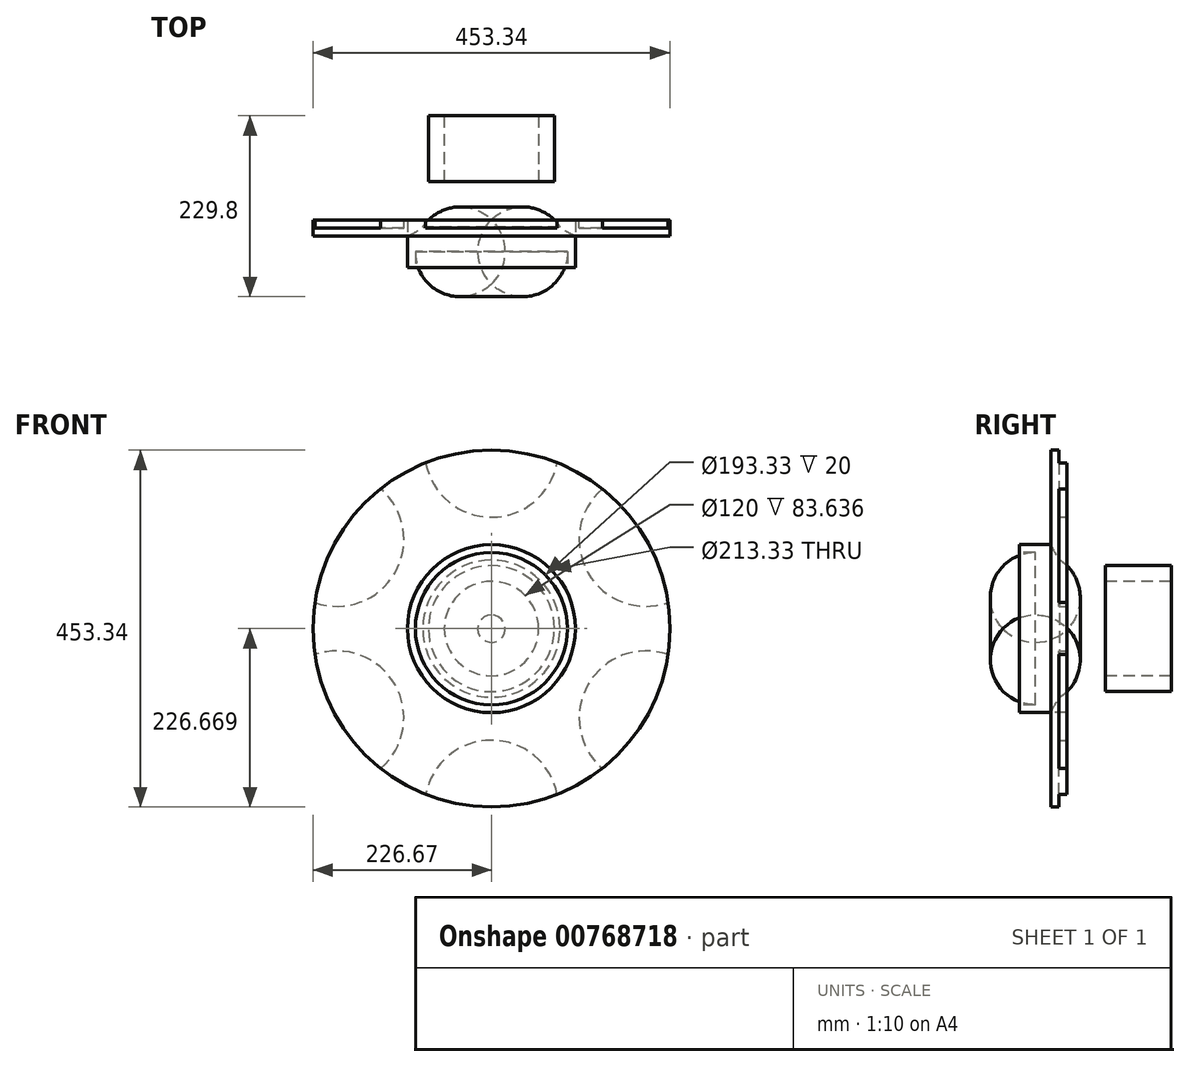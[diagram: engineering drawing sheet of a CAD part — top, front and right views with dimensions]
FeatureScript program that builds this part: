
annotation { "Feature Type Name" : "Feature", "Feature Type Description" : "" }
export const myFeature = defineFeature(function(context is Context, id is Id, definition is map)
    precondition{}
    {
        {
            var Q0;
            Q0=qCreatedBy(makeId("Right.planeOp"),FACE);
            var sketch = newSketch(context, id + "F0", { "sketchPlane" : qUnion([Q0])});
            skLineSegment(sketch, "E0.bottom", {"start": v(-24.37, 154.16) * mm, "end": v(-4.37, 154.16) * mm});
            skLineSegment(sketch, "E0.top", {"start": v(-24.37, 34.16) * mm, "end": v(-4.37, 34.16) * mm});
            skLineSegment(sketch, "E0.left", {"start": v(-24.37, 154.16) * mm, "end": v(-24.37, 34.16) * mm});
            skLineSegment(sketch, "E0.right", {"start": v(-4.37, 154.16) * mm, "end": v(-4.37, 34.16) * mm});
            skLineSegment(sketch, "E1.bottom", {"start": v(-64.37, 24.16) * mm, "end": v(-44.37, 24.16) * mm});
            skLineSegment(sketch, "E1.top", {"start": v(-64.37, 34.16) * mm, "end": v(-44.37, 34.16) * mm});
            skLineSegment(sketch, "E1.left", {"start": v(-64.37, 24.16) * mm, "end": v(-64.37, 34.16) * mm});
            skLineSegment(sketch, "E1.right", {"start": v(-44.37, 24.16) * mm, "end": v(-44.37, 34.16) * mm});
            skLineSegment(sketch, "E2.bottom", {"start": v(44.72, 7.49) * mm, "end": v(128.36, 7.49) * mm});
            skLineSegment(sketch, "E2.top", {"start": v(44.72, -12.51) * mm, "end": v(128.36, -12.51) * mm});
            skLineSegment(sketch, "E2.left", {"start": v(44.72, 7.49) * mm, "end": v(44.72, -12.51) * mm});
            skLineSegment(sketch, "E2.right", {"start": v(128.36, 7.49) * mm, "end": v(128.36, -12.51) * mm});
            skArc(sketch, "E3", {"start": v(-4.37, 34.16) * mm, "mid": v(16.8, 14.59) * mm, "end": v(44.72, 7.49) * mm});
            skArc(sketch, "E4", {"start": v(-24.37, 34.16) * mm, "mid": v(3.04, 0.25) * mm, "end": v(44.72, -12.51) * mm});
            skLineSegment(sketch, "E5", {"start": v(-44.37, 34.16) * mm, "end": v(-24.37, 34.16) * mm});
            skArc(sketch, "E6", {"start": v(-12.75, 14.6) * mm, "mid": v(-27.85, 21.71) * mm, "end": v(-44.37, 24.16) * mm});
            skLineSegment(sketch, "E7", {"start": v(-97.1, -72.51) * mm, "end": v(168.36, -72.51) * mm, "construction": true});
            skLineSegment(sketch, "E8.MirrorCS", {"start": v(-44.37, -169.18) * mm, "end": v(-44.37, -179.18) * mm});
            skLineSegment(sketch, "E9.MirrorCS", {"start": v(-64.37, -169.18) * mm, "end": v(-64.37, -179.18) * mm});
            skArc(sketch, "E10.MirrorCS", {"start": v(-12.75, -159.62) * mm, "mid": v(-27.85, -166.74) * mm, "end": v(-44.37, -169.18) * mm});
            skLineSegment(sketch, "E11.MirrorCS", {"start": v(-44.37, -179.18) * mm, "end": v(-24.37, -179.18) * mm});
            skArc(sketch, "E12.MirrorCS", {"start": v(-24.37, -179.18) * mm, "mid": v(3.04, -145.27) * mm, "end": v(44.72, -132.51) * mm});
            skArc(sketch, "E13.MirrorCS", {"start": v(-4.37, -179.18) * mm, "mid": v(16.8, -159.6) * mm, "end": v(44.72, -152.51) * mm});
            skLineSegment(sketch, "E14.MirrorCS", {"start": v(128.36, -152.51) * mm, "end": v(128.36, -132.51) * mm});
            skLineSegment(sketch, "E15.MirrorCS", {"start": v(44.72, -152.51) * mm, "end": v(44.72, -132.51) * mm});
            skLineSegment(sketch, "E16.MirrorCS", {"start": v(44.72, -132.51) * mm, "end": v(128.36, -132.51) * mm});
            skLineSegment(sketch, "E17.MirrorCS", {"start": v(44.72, -152.51) * mm, "end": v(128.36, -152.51) * mm});
            skLineSegment(sketch, "E18.MirrorCS", {"start": v(-64.37, -179.18) * mm, "end": v(-44.37, -179.18) * mm});
            skLineSegment(sketch, "E19.MirrorCS", {"start": v(-64.37, -169.18) * mm, "end": v(-44.37, -169.18) * mm});
            skLineSegment(sketch, "E20.MirrorCS", {"start": v(-4.37, -299.18) * mm, "end": v(-4.37, -179.18) * mm});
            skLineSegment(sketch, "E21.MirrorCS", {"start": v(-24.37, -299.18) * mm, "end": v(-24.37, -179.18) * mm});
            skLineSegment(sketch, "E22.MirrorCS", {"start": v(-24.37, -299.18) * mm, "end": v(-4.37, -299.18) * mm});
            skLineSegment(sketch, "E23.MirrorCS", {"start": v(-24.37, -179.18) * mm, "end": v(-4.37, -179.18) * mm});
            skSolve(sketch);
        }
        {
            var Q0;
            Q0=makeQuery(id+"F0.imprint","IMPRINT",FACE,{"disambiguationData":[TD([[makeQuery(id+"F0.imprint","IMPRINT",EDGE,{"derivedFrom":sQuery(id+"F0.wireOp",EDGE,"E8.MirrorCS")}),-1.0]])]});
            var Q1;
            Q1=makeQuery(id+"F0.imprint","IMPRINT",FACE,{"disambiguationData":[TD([[makeQuery(id+"F0.imprint","IMPRINT",EDGE,{"derivedFrom":sQuery(id+"F0.wireOp",EDGE,"E8.MirrorCS")}),1.0]])]});
            var Q2;
            Q2=makeQuery(id+"F0.imprint","IMPRINT",FACE,{"disambiguationData":[TD([[makeQuery(id+"F0.imprint","IMPRINT",EDGE,{"derivedFrom":sQuery(id+"F0.wireOp",EDGE,"E20.MirrorCS")}),1.0]])]});
            var Q3;
            Q3=makeQuery(id+"F0.imprint","IMPRINT",FACE,{"disambiguationData":[TD([[makeQuery(id+"F0.imprint","IMPRINT",EDGE,{"derivedFrom":sQuery(id+"F0.wireOp",EDGE,"E14.MirrorCS")}),1.0]])]});
            var Q4;
            Q4=makeQuery(id+"F0.imprint","IMPRINT",FACE,{"disambiguationData":[TD([[makeQuery(id+"F0.imprint","IMPRINT",EDGE,{"derivedFrom":sQuery(id+"F0.wireOp",EDGE,"E13.MirrorCS")}),1.0]])]});
            var Q5;
            Q5=sQuery(id+"F0.wireOp",EDGE,"E7");
            revolve(context, id + "F1", {"surfaceOperationType" : NewSurfaceOperationType.NEW, "entities" : qUnion([Q0, Q1, Q2, Q3, Q4]), "axis" : qUnion([Q5]), "revolveType" : RevolveType.FULL});
        }
        {
            var Q0;
            Q0=makeQuery(id+"F1.opRevolve","SWEPT_FACE",FACE,{"disambiguationData":[OSD([sQuery(id+"F0.wireOp",EDGE,"E20.MirrorCS")])]});
            var sketch = newSketch(context, id + "F2", { "sketchPlane" : qUnion([Q0])});
            skArc(sketch, "E24", {"start": v(84.96, -296.72) * mm, "mid": v(-0.64, -214.18) * mm, "end": v(-85, -298) * mm});
            skArc(sketch, "E25.1.0", {"start": v(236.66, -111.04) * mm, "mid": v(122.37, -143.9) * mm, "end": v(152.79, -258.86) * mm});
            skArc(sketch, "E25.2.0", {"start": v(151.7, 113.18) * mm, "mid": v(123, -2.23) * mm, "end": v(237.78, -33.37) * mm});
            skArc(sketch, "E25.3.0", {"start": v(-84.96, 151.7) * mm, "mid": v(0.64, 69.16) * mm, "end": v(85, 152.98) * mm});
            skArc(sketch, "E25.4.0", {"start": v(-236.66, -33.99) * mm, "mid": v(-122.37, -1.12) * mm, "end": v(-152.79, 113.84) * mm});
            skArc(sketch, "E25.5.0", {"start": v(-151.7, -258.2) * mm, "mid": v(-123, -142.8) * mm, "end": v(-237.78, -111.65) * mm});
            skPoint(sketch, "E25.center", {"position": v(0, -72.51) * mm});
            skSolve(sketch);
        }
        {
            var Q0;
            {var subQ0=sQuery(id+"F2.wireOp",EDGE,"E24");var subQ1=makeQuery(id+"F1.opRevolve","SWEPT_EDGE",EDGE,{"disambiguationData":[OSD([sQuery(id+"F0.wireOp",EDGE,"E20.MirrorCS"),sQuery(id+"F0.wireOp",EDGE,"E22.MirrorCS")])]});var subQ2=makeQuery(id+"F2.imprint","INTERSECT",VERTEX,{"disambiguationData":[OD(0.0)],"derivedFrom":[subQ1,subQ0]});Q0=makeQuery(id+"F2.imprint","IMPRINT",FACE,{"disambiguationData":[TD([[makeQuery(id+"F2.imprint","IMPRINT",EDGE,{"disambiguationData":[TD([[subQ2,-1.0]])],"derivedFrom":subQ0}),1.0]])]});}
            extrude(context, id + "F3", {"entities" : qUnion([Q0]), "operationType" : NewBodyOperationType.REMOVE, "oppositeDirection" : true, "depth" : 10 * mm, "offsetDistance" : 25 * mm});
        }
        {
            var Q0;
            {var subQ0=sQuery(id+"F2.wireOp",EDGE,"E25.5.0");var subQ1=makeQuery(id+"F1.opRevolve","SWEPT_EDGE",EDGE,{"disambiguationData":[OSD([sQuery(id+"F0.wireOp",EDGE,"E20.MirrorCS"),sQuery(id+"F0.wireOp",EDGE,"E22.MirrorCS")])]});var subQ2=makeQuery(id+"F2.imprint","INTERSECT",VERTEX,{"disambiguationData":[OD(0.0)],"derivedFrom":[subQ1,subQ0]});Q0=makeQuery(id+"F2.imprint","IMPRINT",FACE,{"disambiguationData":[TD([[makeQuery(id+"F2.imprint","IMPRINT",EDGE,{"disambiguationData":[TD([[subQ2,-1.0]])],"derivedFrom":subQ0}),1.0]])]});}
            var Q1;
            {var subQ0=sQuery(id+"F2.wireOp",EDGE,"E25.4.0");var subQ1=makeQuery(id+"F1.opRevolve","SWEPT_EDGE",EDGE,{"disambiguationData":[OSD([sQuery(id+"F0.wireOp",EDGE,"E20.MirrorCS"),sQuery(id+"F0.wireOp",EDGE,"E22.MirrorCS")])]});var subQ2=makeQuery(id+"F2.imprint","INTERSECT",VERTEX,{"disambiguationData":[OD(0.0)],"derivedFrom":[subQ1,subQ0]});Q1=makeQuery(id+"F2.imprint","IMPRINT",FACE,{"disambiguationData":[TD([[makeQuery(id+"F2.imprint","IMPRINT",EDGE,{"disambiguationData":[TD([[subQ2,1.0]])],"derivedFrom":subQ0}),1.0]])]});}
            var Q2;
            {var subQ0=sQuery(id+"F2.wireOp",EDGE,"E25.3.0");var subQ1=makeQuery(id+"F1.opRevolve","SWEPT_EDGE",EDGE,{"disambiguationData":[OSD([sQuery(id+"F0.wireOp",EDGE,"E20.MirrorCS"),sQuery(id+"F0.wireOp",EDGE,"E22.MirrorCS")])]});var subQ2=makeQuery(id+"F2.imprint","INTERSECT",VERTEX,{"disambiguationData":[OD(0.0)],"derivedFrom":[subQ1,subQ0]});Q2=makeQuery(id+"F2.imprint","IMPRINT",FACE,{"disambiguationData":[TD([[makeQuery(id+"F2.imprint","IMPRINT",EDGE,{"disambiguationData":[TD([[subQ2,1.0]])],"derivedFrom":subQ0}),1.0]])]});}
            var Q3;
            {var subQ0=sQuery(id+"F2.wireOp",EDGE,"E25.2.0");var subQ1=makeQuery(id+"F1.opRevolve","SWEPT_EDGE",EDGE,{"disambiguationData":[OSD([sQuery(id+"F0.wireOp",EDGE,"E20.MirrorCS"),sQuery(id+"F0.wireOp",EDGE,"E22.MirrorCS")])]});var subQ2=makeQuery(id+"F2.imprint","INTERSECT",VERTEX,{"disambiguationData":[OD(0.0)],"derivedFrom":[subQ1,subQ0]});Q3=makeQuery(id+"F2.imprint","IMPRINT",FACE,{"disambiguationData":[TD([[makeQuery(id+"F2.imprint","IMPRINT",EDGE,{"disambiguationData":[TD([[subQ2,1.0]])],"derivedFrom":subQ0}),1.0]])]});}
            var Q4;
            {var subQ0=sQuery(id+"F2.wireOp",EDGE,"E25.1.0");var subQ1=makeQuery(id+"F1.opRevolve","SWEPT_EDGE",EDGE,{"disambiguationData":[OSD([sQuery(id+"F0.wireOp",EDGE,"E20.MirrorCS"),sQuery(id+"F0.wireOp",EDGE,"E22.MirrorCS")])]});var subQ2=makeQuery(id+"F2.imprint","INTERSECT",VERTEX,{"disambiguationData":[OD(0.0)],"derivedFrom":[subQ1,subQ0]});Q4=makeQuery(id+"F2.imprint","IMPRINT",FACE,{"disambiguationData":[TD([[makeQuery(id+"F2.imprint","IMPRINT",EDGE,{"disambiguationData":[TD([[subQ2,-1.0]])],"derivedFrom":subQ0}),1.0]])]});}
            extrude(context, id + "F4", {"entities" : qUnion([Q0, Q1, Q2, Q3, Q4]), "operationType" : NewBodyOperationType.REMOVE, "oppositeDirection" : true, "depth" : 10 * mm, "offsetDistance" : 25 * mm});
        }
    });
